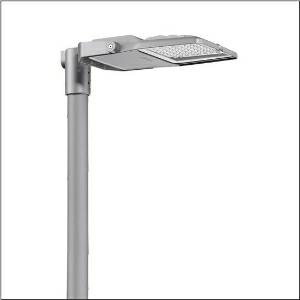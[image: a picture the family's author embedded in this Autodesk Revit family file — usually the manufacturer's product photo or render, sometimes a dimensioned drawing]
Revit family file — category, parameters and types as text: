
# Revit family: floodlight_fl_21_mini___pl61_5xa7776d2c3a_4c8f
name_source: partatom
category: Lighting Fixtures
units: mm (PartAtom-declared; Revit-internal decimal feet)

## family parameters
Cut with Voids When Loaded = No
Host = Face
Light Source = No
Part Type = Normal
Room Calculation Point = No
Round Connector Dimension = Use Diameter
Shared = No

## types (1)
- --- (1 x LED, 17510 lm, 142.9 W, 3000K)
    Apparent Load = 143 VA
    CIE Flux Codes = 33 65 98 100 100
    Color Rendering = 70
    Color Temperature = 3000K
    Default Elevation = 1800 mm
    Description = Floodlight FL 21 mini, floodlight, primary light control with lens, of PMMA, primary optical cover: protective disc, of toughened safety glass, transparent, light distribution: PL61, light emission: direct distribution, installation type: surface-mounted, LED, High Power LED, rated luminous flux: 17.510lm, luminous efficacy: 123lm/W, light colour: 730, colour temperature: 3000K, control gear: Smart Interface (Zhaga), control: flexible luminous flux parameterisation, time-dependent luminous flux control, constant luminous flux control, overheat protection, pre-setting: logarithmic dimming characteristic, with terminal, 6-pole, mains connection: 220..240V, AC, 50/60Hz, start of lifetime: 143W, end of service life: 151W, reduction: 63W, luminaire housing, of diecast aluminium, powder-coated, Siteco® metallic grey (DB 702S), corrosivity category C5 mid according to DIN EN ISO 12944, suitable for swimming pools, chlorine-resistant, sealing non-destructively replaceable, please order mast flange separately, mast bracket, of steel, galvanised, powder-coated, Siteco® metallic grey (DB 702S), Smart Interface below and above, protection rating (complete): IP66, insulation class (complete): insulation class II (safety insulation), certification: CE, ENEC, VDE, protection symbol: D, impact resistance: IK08, permissible operating ambient temperature: -40..+40°C, permissible operating ambient temperature for outdoor applications: -40..+50°C, standard: DIN EN 12944, LABS conformity tested according to VDMA 24364:2018-05, packaging unit: 1 piece

Light Distribution: PL61
    Height = 70 mm
    Lamp = 1 x LED
    Lamp Light Flux = 17510 lm
    Lamp Power = 142.9 W
    Lamp count = 1
    Length = 485 mm
    Luminous efficacy = 123 lm/W
    Manufacturer = Siteco
    ModVariant = No
    Model = 5XA7776D2C3A
    Number of Poles = 1
    OnlyDefault = Yes
    Power Factor = 1
    Product Name = Floodlight FL 21 mini | PL61
    Product group = floodlight | pylon annexe
    ProductGroupID = 6200
    Protection Class = Protection class II
    Protection Degree = IP 66
    RLX_Detail_Level = 1
    RLX_Emergency_Light_Flux = 0 lm
    RLX_Emergency_Type = 0
    RLX_Emergency_Type_DB = No
    RlxData = <blob elided: 101425 chars, md5=96cc62f6>
    Socket = socket
    Standby Power = 0 W
    System Light Flux = 17510 lm
    System Power = 143 W
    Type Comments = factory setting: luminous flux: 100 % | dim-lin: 254 | 730 mA
    Type Image = l_1007125.jpg
    URL = http://relux.com
    VarID = @adj_171854
    Voltage = 0 V
    Weight = 0.00 kg
    Width = 337 mm

## geometry (parser evidence)
native form markers: Blend x4, Sweep x12
no freeform markers — native parametric forms only
